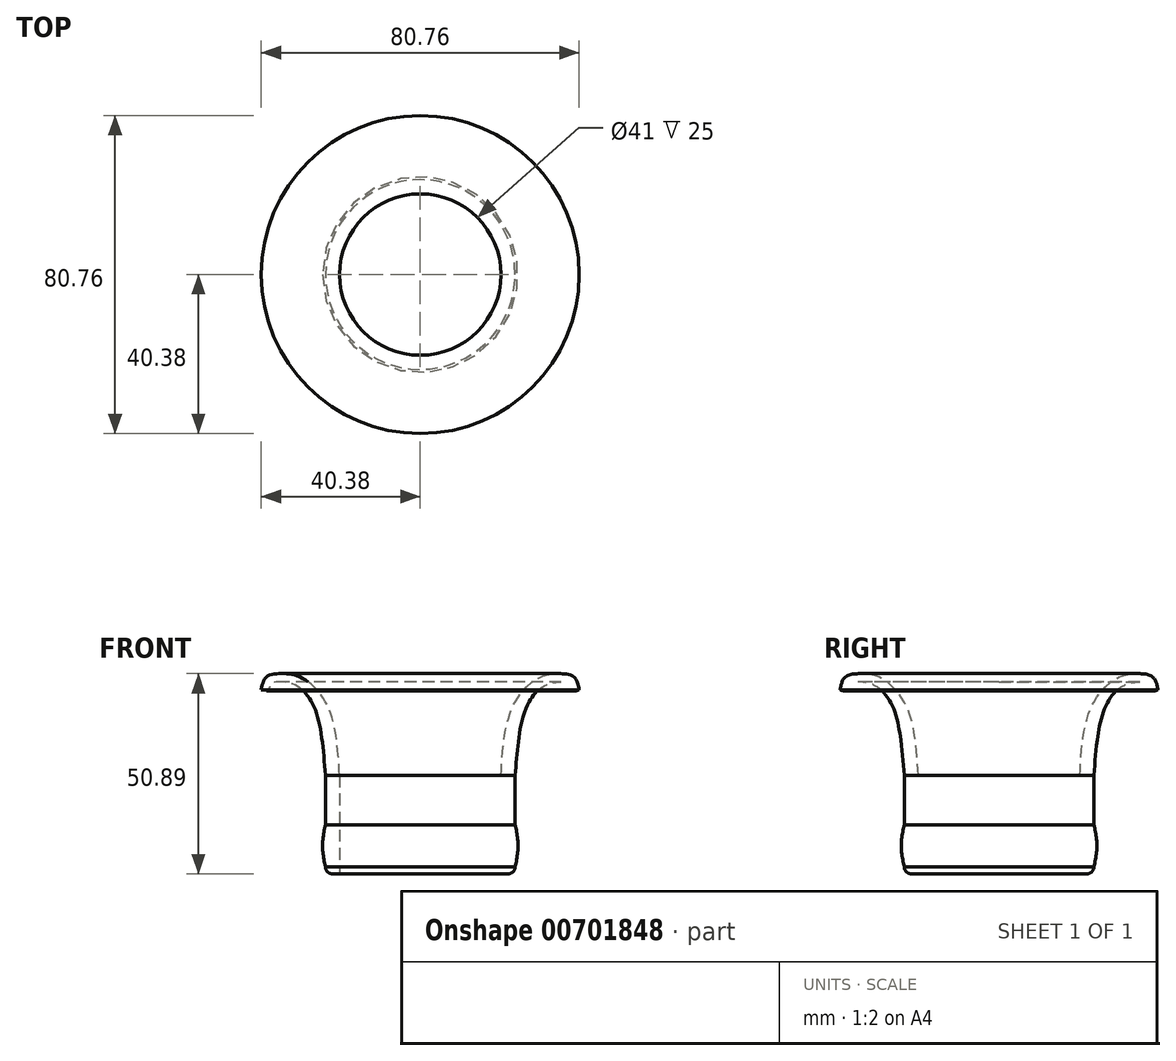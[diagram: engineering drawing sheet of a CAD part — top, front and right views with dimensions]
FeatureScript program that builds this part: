
annotation { "Feature Type Name" : "Feature", "Feature Type Description" : "" }
export const myFeature = defineFeature(function(context is Context, id is Id, definition is map)
    precondition{}
    {
        {
            var Q0;
            Q0=qCreatedBy(makeId("Front.planeOp"),FACE);
            var sketch = newSketch(context, id + "F0", { "sketchPlane" : qUnion([Q0])});
            skLineSegment(sketch, "E0.bottom", {"start": v(20.5, 0) * mm, "end": v(22.3, 0) * mm});
            skLineSegment(sketch, "E0.left", {"start": v(20.5, 0) * mm, "end": v(20.5, 25) * mm});
            skArc(sketch, "E1.filletArc", {"start": v(22.3, 0) * mm, "mid": v(23.57, 0.53) * mm, "end": v(24.1, 1.8) * mm});
            skLineSegment(sketch, "E2", {"start": v(24.1, 25) * mm, "end": v(24.1, 12.5) * mm});
            skFitSpline(sketch, "E3", {"points": [v(24.1, 12.5) * mm, v(24.85, 7.15) * mm, v(24.1, 1.8) * mm], "startDerivative": vector(2.25, -10.7) * mm, "endDerivative": vector(-2.25, -10.7) * mm});
            skFitSpline(sketch, "E4", {"points": [v(20.5, 25) * mm, v(23.62, 42.8) * mm, v(30.5, 50) * mm, v(35.34, 50.89) * mm, v(39.1, 50) * mm, v(40.38, 46.77) * mm], "startDerivative": vector(3.9, 61.95) * mm, "endDerivative": vector(5.16, -27.32) * mm});
            skFitSpline(sketch, "E5", {"points": [v(24.1, 25) * mm, v(26.87, 42.13) * mm, v(31.46, 47.76) * mm, v(35.45, 48.76) * mm, v(38.06, 48.1) * mm, v(38.7, 46.54) * mm, v(40.38, 46.77) * mm], "startDerivative": vector(4.67, 60.72) * mm, "endDerivative": vector(20.54, 7.72) * mm});
            skLineSegment(sketch, "E6", {"start": v(0, 0) * mm, "end": v(0, 61.34) * mm});
            skSolve(sketch);
        }
        {
            var Q0;
            Q0=makeQuery(id+"F0.imprint","IMPRINT",FACE,{"disambiguationData":[TD([[makeQuery(id+"F0.imprint","IMPRINT",EDGE,{"derivedFrom":sQuery(id+"F0.wireOp",EDGE,"E0.bottom")}),1.0]])]});
            var Q1;
            Q1=sQuery(id+"F0.wireOp",EDGE,"E6");
            revolve(context, id + "F1", {"entities" : qUnion([Q0]), "axis" : qUnion([Q1]), "revolveType" : RevolveType.FULL});
        }
    });
